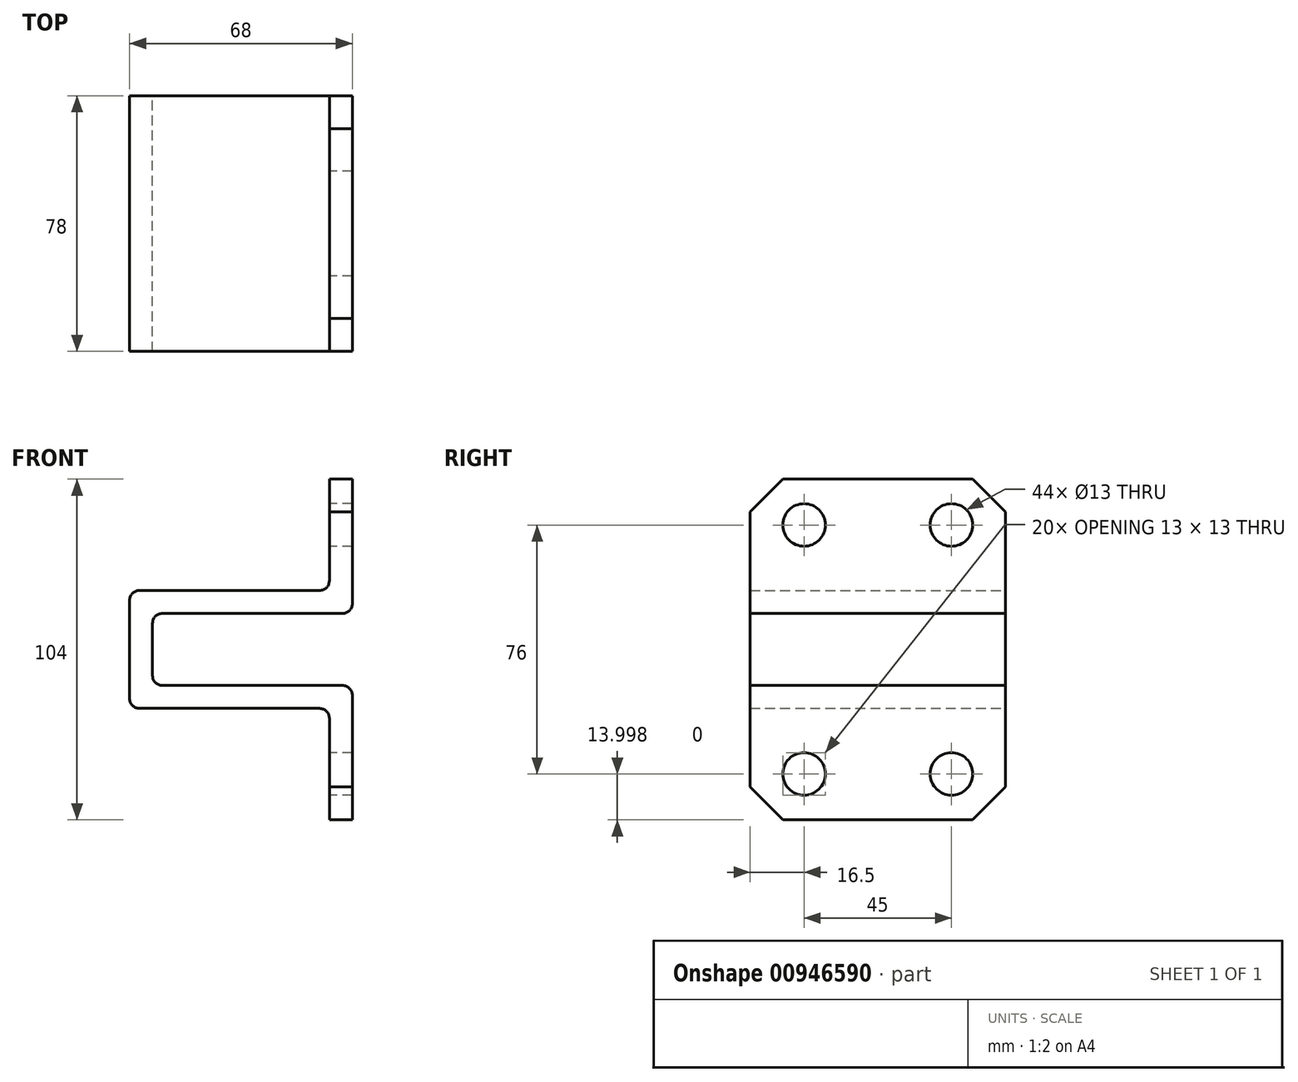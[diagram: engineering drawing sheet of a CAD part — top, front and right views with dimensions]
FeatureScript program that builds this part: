
annotation { "Feature Type Name" : "Feature", "Feature Type Description" : "" }
export const myFeature = defineFeature(function(context is Context, id is Id, definition is map)
    precondition{}
    {
        {
            var Q0;
            Q0=qCreatedBy(makeId("Front.planeOp"),FACE);
            var sketch = newSketch(context, id + "F0", { "sketchPlane" : qUnion([Q0])});
            skLineSegment(sketch, "E0", {"start": v(0, 88.16) * mm, "end": v(0, 50.16) * mm});
            skLineSegment(sketch, "E1", {"start": v(-3, 47.16) * mm, "end": v(-58, 47.16) * mm});
            skLineSegment(sketch, "E2", {"start": v(-61, 44.16) * mm, "end": v(-61, 28.16) * mm});
            skLineSegment(sketch, "E3", {"start": v(-58, 25.16) * mm, "end": v(-3, 25.16) * mm});
            skLineSegment(sketch, "E4", {"start": v(0, 22.16) * mm, "end": v(0, -15.84) * mm});
            skLineSegment(sketch, "E5", {"start": v(0, -15.84) * mm, "end": v(-7, -15.84) * mm});
            skLineSegment(sketch, "E6", {"start": v(-7, -15.84) * mm, "end": v(-7, 15.16) * mm});
            skLineSegment(sketch, "E7", {"start": v(-10, 18.16) * mm, "end": v(-65, 18.16) * mm});
            skLineSegment(sketch, "E8", {"start": v(-68, 21.16) * mm, "end": v(-68, 51.16) * mm});
            skLineSegment(sketch, "E9", {"start": v(-65, 54.16) * mm, "end": v(-10, 54.16) * mm});
            skLineSegment(sketch, "E10", {"start": v(0, 88.16) * mm, "end": v(-7, 88.16) * mm});
            skLineSegment(sketch, "E11", {"start": v(-7, 88.16) * mm, "end": v(-7, 57.16) * mm});
            skPoint(sketch, "E12.visualSharp", {"position": v(-68, 54.16) * mm});
            skArc(sketch, "E12.filletArc", {"start": v(-65, 54.16) * mm, "mid": v(-67.12, 53.28) * mm, "end": v(-68, 51.16) * mm});
            skPoint(sketch, "E13.visualSharp", {"position": v(-61, 47.16) * mm});
            skArc(sketch, "E13.filletArc", {"start": v(-58, 47.16) * mm, "mid": v(-60.12, 46.28) * mm, "end": v(-61, 44.16) * mm});
            skPoint(sketch, "E14.visualSharp", {"position": v(-61, 25.16) * mm});
            skArc(sketch, "E14.filletArc", {"start": v(-61, 28.16) * mm, "mid": v(-60.12, 26.04) * mm, "end": v(-58, 25.16) * mm});
            skPoint(sketch, "E15.visualSharp", {"position": v(-68, 18.16) * mm});
            skArc(sketch, "E15.filletArc", {"start": v(-68, 21.16) * mm, "mid": v(-67.12, 19.04) * mm, "end": v(-65, 18.16) * mm});
            skPoint(sketch, "E16.visualSharp", {"position": v(-7, 18.16) * mm});
            skArc(sketch, "E16.filletArc", {"start": v(-7, 15.16) * mm, "mid": v(-7.88, 17.28) * mm, "end": v(-10, 18.16) * mm});
            skPoint(sketch, "E17.visualSharp", {"position": v(0, 25.16) * mm});
            skArc(sketch, "E17.filletArc", {"start": v(0, 22.16) * mm, "mid": v(-0.88, 24.28) * mm, "end": v(-3, 25.16) * mm});
            skPoint(sketch, "E18.visualSharp", {"position": v(0, 47.16) * mm});
            skArc(sketch, "E18.filletArc", {"start": v(-3, 47.16) * mm, "mid": v(-0.88, 48.04) * mm, "end": v(0, 50.16) * mm});
            skPoint(sketch, "E19.visualSharp", {"position": v(-7, 54.16) * mm});
            skArc(sketch, "E19.filletArc", {"start": v(-10, 54.16) * mm, "mid": v(-7.88, 55.04) * mm, "end": v(-7, 57.16) * mm});
            skSolve(sketch);
        }
        {
            var Q0;
            Q0 = qSketchRegion(id + "F0", true);
            extrude(context, id + "F1", {"entities" : qUnion([Q0]), "depth" : 78 * mm, "offsetDistance" : 25 * mm});
        }
        {
            var Q0;
            Q0=makeQuery(id+"F1.opExtrude","SWEPT_FACE",FACE,{"disambiguationData":[OSD([sQuery(id+"F0.wireOp",EDGE,"E11")])]});
            var sketch = newSketch(context, id + "F2", { "sketchPlane" : qUnion([Q0])});
            skCircle(sketch, "E20", {"center": v(61.5, 74.16) * mm, "radius": 6.5 * mm});
            skCircle(sketch, "E21", {"center": v(16.5, 74.16) * mm, "radius": 6.5 * mm});
            skCircle(sketch, "E22", {"center": v(16.5, -1.84) * mm, "radius": 6.5 * mm});
            skCircle(sketch, "E23", {"center": v(61.5, -1.84) * mm, "radius": 6.5 * mm});
            skLineSegment(sketch, "E24", {"start": v(68, 88.16) * mm, "end": v(78, 78.16) * mm});
            skLineSegment(sketch, "E25", {"start": v(68, 88.16) * mm, "end": v(78, 88.16) * mm});
            skLineSegment(sketch, "E26", {"start": v(78, 88.16) * mm, "end": v(78, 78.16) * mm});
            skLineSegment(sketch, "E27", {"start": v(0, 78.16) * mm, "end": v(10, 88.16) * mm});
            skLineSegment(sketch, "E28", {"start": v(10, 88.16) * mm, "end": v(0, 88.16) * mm});
            skLineSegment(sketch, "E29", {"start": v(0, 88.16) * mm, "end": v(0, 78.16) * mm});
            skLineSegment(sketch, "E30", {"start": v(68, -15.84) * mm, "end": v(78, -5.84) * mm});
            skLineSegment(sketch, "E31", {"start": v(78, -5.84) * mm, "end": v(78, -15.84) * mm});
            skLineSegment(sketch, "E32", {"start": v(78, -15.84) * mm, "end": v(68, -15.84) * mm});
            skLineSegment(sketch, "E33", {"start": v(10, -15.84) * mm, "end": v(0, -5.84) * mm});
            skLineSegment(sketch, "E34", {"start": v(0, -5.84) * mm, "end": v(0, -15.84) * mm});
            skLineSegment(sketch, "E35", {"start": v(0, -15.84) * mm, "end": v(10, -15.84) * mm});
            skSolve(sketch);
        }
        {
            var Q0;
            Q0 = qSketchRegion(id + "F2", true);
            extrude(context, id + "F3", {"entities" : qUnion([Q0]), "operationType" : NewBodyOperationType.REMOVE, "oppositeDirection" : true, "depth" : 25 * mm, "offsetDistance" : 25 * mm});
        }
    });
